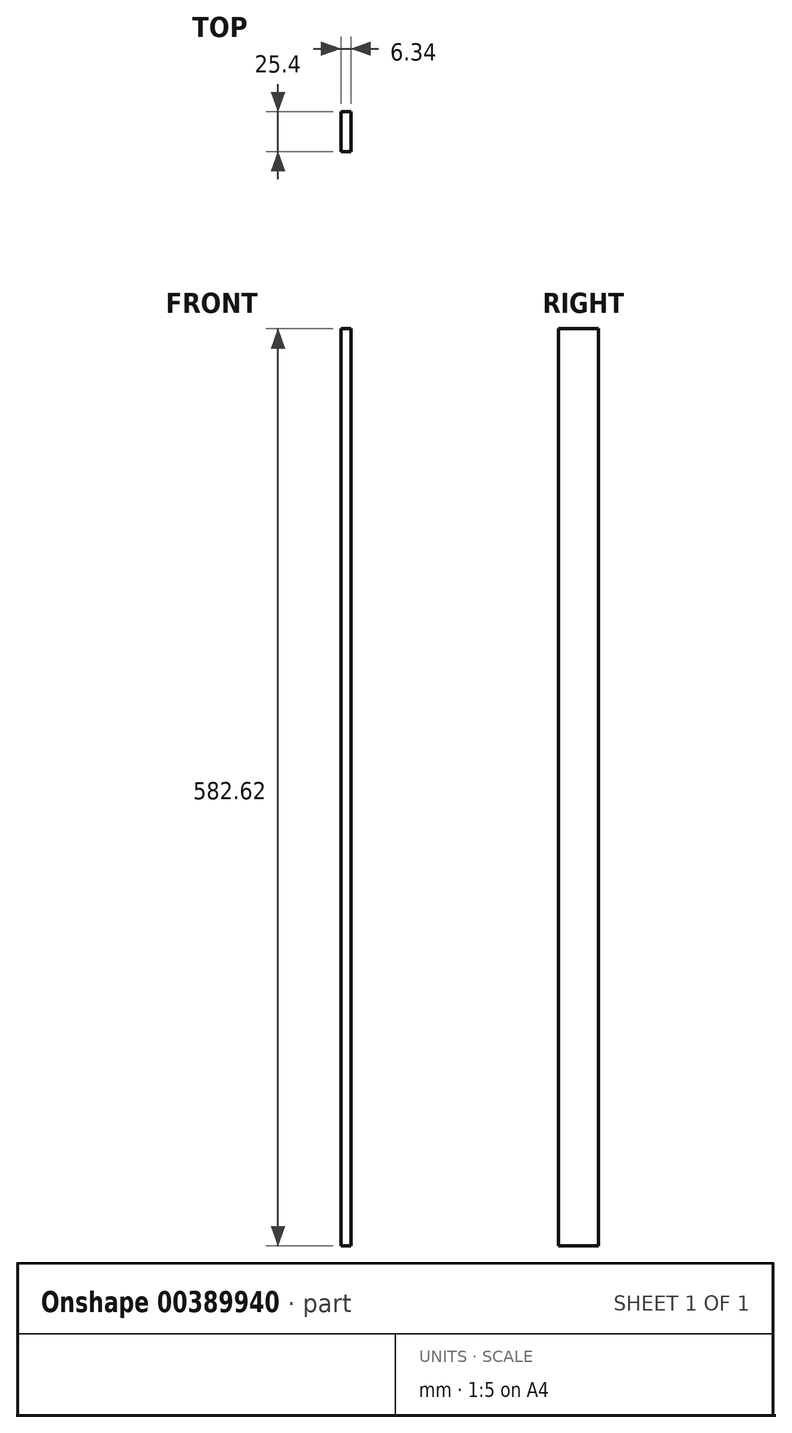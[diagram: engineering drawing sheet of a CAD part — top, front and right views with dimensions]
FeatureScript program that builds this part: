
annotation { "Feature Type Name" : "Feature", "Feature Type Description" : "" }
export const myFeature = defineFeature(function(context is Context, id is Id, definition is map)
    precondition{}
    {
        {
            var Q0;
            Q0=qCreatedBy(makeId("Front.planeOp"),FACE);
            var sketch = newSketch(context, id + "F0", { "sketchPlane" : qUnion([Q0])});
            skLineSegment(sketch, "E0.bottom", {"start": v(3.17, -291.3) * mm, "end": v(-3.18, -291.3) * mm});
            skLineSegment(sketch, "E0.top", {"start": v(3.18, 291.3) * mm, "end": v(-3.17, 291.3) * mm});
            skLineSegment(sketch, "E0.left", {"start": v(3.17, -291.3) * mm, "end": v(3.18, 291.3) * mm});
            skLineSegment(sketch, "E0.right", {"start": v(-3.18, -291.3) * mm, "end": v(-3.17, 291.3) * mm});
            skPoint(sketch, "E0.middle", {"position": v(0, 0) * mm});
            skSolve(sketch);
        }
        {
            var Q0;
            Q0 = qSketchRegion(id + "F0", true);
            extrude(context, id + "F1", {"entities" : qUnion([Q0]), "depth" : 25.4 * mm});
        }
    });
